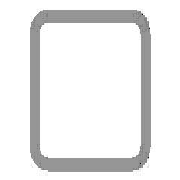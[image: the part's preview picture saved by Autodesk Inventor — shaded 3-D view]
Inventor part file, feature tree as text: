
AUTODESK INVENTOR PART (.ipt)
format: ipt  version: 2025 (Build 290162010, 162A)  size: 133,120 bytes
history: native  units: mm (DEFAULTED — no unit token found)
features: other x4, sketch x1, plane x1
ambient origin geometry x8: Origin, YZ Plane, XZ Plane, XY Plane, X Axis, Y Axis, Z Axis, Center Point
bodies: Solid1 (feature_tree), Body (feature_tree)
feature tree (6):
  parser-record x1  (decoder bookkeeping rows leaked as tree rows — omitted from the tree; the rows remain in map.json)
  other  "Driven Length"
  other  "Start Plane"
  other  "End Plane"
  sketch  "Sketch3"  dims[d3=840.0mm d4=0.0mm d7=8.0mm d9=50.0mm d11=50.0mm d12=4.0mm d13=-0.0mm d14=840.0mm d15=25.0mm d16=25.0mm d17=90.0deg d18=840.0mm]
  plane  "Work Plane3"
